# Revit family: Toilet_Seat-Round-American_Standard-Cardiff-5257A65MT_Series
name_source: partatom
category: Specialty Equipment
revit_build: Autodesk Revit 2018 (Build: 20170223_1515(x64)
units: mm (PartAtom-declared; Revit-internal decimal feet)

## family parameters
Always vertical = No
Cut with Voids When Loaded = No
OmniClass Number = 23.45.05.21.14.11
OmniClass Title = Water Closet Seats
Part Type = Normal
Room Calculation Point = No
Round Connector Dimension = Use Diameter
Shared = Yes
Work Plane-Based = Yes

## types (3) — shared parameters
760219-100.0070A Bottom Mounting Kit = No
760227-100.0070A Top Mounting Kit = No
Assembly Code = C1030200
Default Elevation = 0"
Description = Cardiff™ Slow-Close Elongated Toilet Seat
Height = 2 1/4"
Installation Type = Surface Mounted
Length = 17 3/8"
Manufacturer = American Standard
Product Documentation Link = https://americanstandard.box.com
Product Page URL = https://www.americanstandard-us.com
URL = http://www.americanstandard-us.com
Width = 13 7/8"

## per-type parameters (varying)
| type | Finish | Material |
| 5257A65MT.020 | Plastic-American Standard-020-White | Plastic-American Standard-020-White |
| 5257A65MT.021 | Plastic-American Standard-021-Bone | Plastic-American Standard-021-Bone |
| 5257A65MT.222 | Plastic-American Standard-222-Linen | Plastic-American Standard-222-Linen |

note: column(s) folded — value = type name in every type: Model

## geometry (parser evidence)
native form markers: Sweep x2
no freeform markers — native parametric forms only
